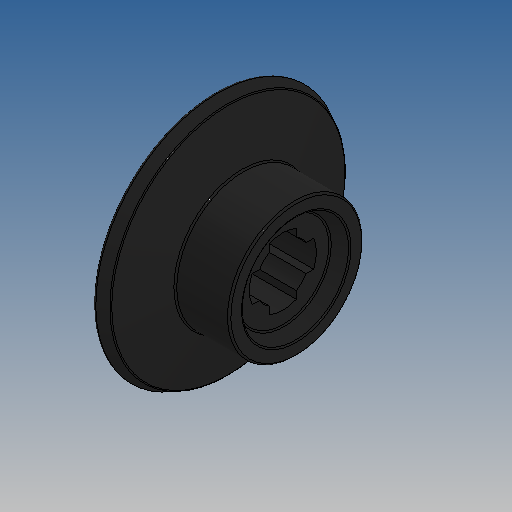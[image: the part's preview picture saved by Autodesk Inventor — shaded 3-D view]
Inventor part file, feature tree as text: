
AUTODESK INVENTOR PART (.ipt)
format: ipt  version: 2025 (Build 290162010, 162A)  size: 209,920 bytes
history: native  units: mm
features: sketch x2, revolve x1, fillet x1, extrude x1, pattern_circular x1
ambient origin geometry x8: Origin, YZ Plane, XZ Plane, XY Plane, X Axis, Y Axis, Z Axis, Center Point
bodies: Volumenkörper1 (feature_tree)
feature tree (6):
  revolve  "Umdrehung1"
  fillet  "Rundung1"  Radius=0.1mm
  extrude  "Extrusion1"  Depth=8.0mm
  pattern_circular  "Runde Anordnung1"  [2 undecoded]
  sketch  "Skizze1"  dims[d1=14.6mm d2=8.0mm]
  sketch  "Skizze2"  dims[d3=4.8mm d4=3.2mm d5=11.082841mm d6=18.50049mm d7=360.0deg d8=0.1mm d9=4.8mm d10=0.1mm d11=0.8mm d12=12.8mm d13=0.8mm d14=4.625123mm d15=5.6mm d16=3.2mm d17=1.6mm d18=2.0mm d19=10.0mm d20=0.0mm d21=40.0mm d22=360.0deg]
note: 2 required parameter values undecoded (feature->parameter linkage not recoverable at this tier; creation-order binding heuristic only, values carry confidence <= 0.55)
